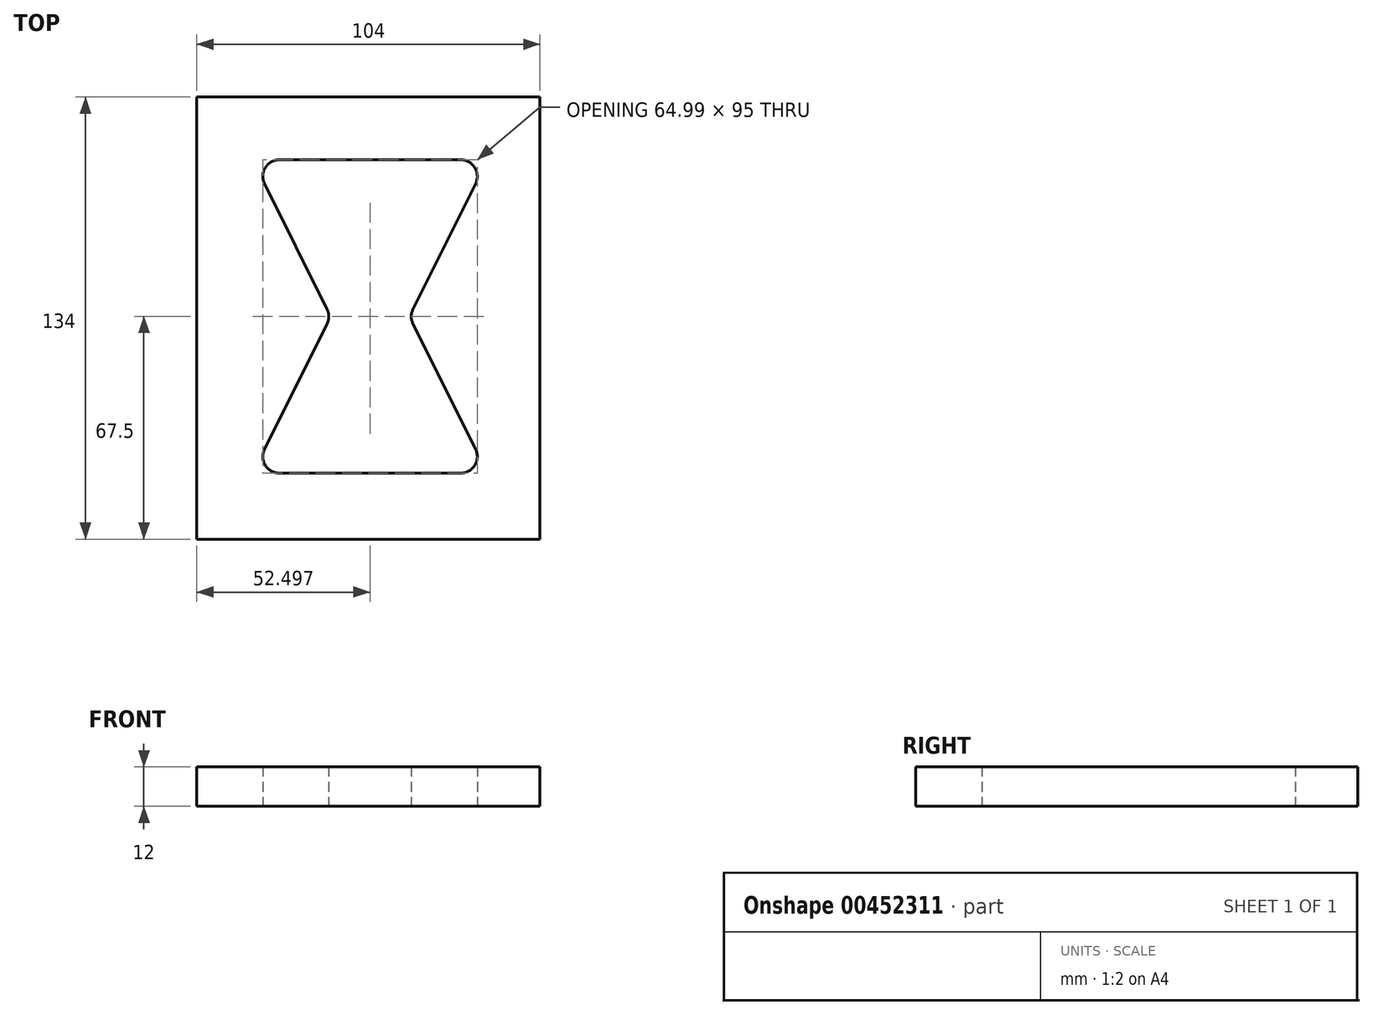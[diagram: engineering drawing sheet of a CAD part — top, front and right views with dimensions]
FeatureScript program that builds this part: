
annotation { "Feature Type Name" : "Feature", "Feature Type Description" : "" }
export const myFeature = defineFeature(function(context is Context, id is Id, definition is map)
    precondition{}
    {
        {
            var Q0;
            Q0=qCreatedBy(makeId("Top.planeOp"),FACE);
            var sketch = newSketch(context, id + "F0", { "sketchPlane" : qUnion([Q0])});
            skLineSegment(sketch, "E0", {"start": v(-3.13, 0) * mm, "end": v(-58.13, 0) * mm});
            skLineSegment(sketch, "E1", {"start": v(-58.13, 95) * mm, "end": v(-3.13, 95) * mm});
            skLineSegment(sketch, "E2", {"start": v(-18.72, 47.5) * mm, "end": v(-42.55, 47.5) * mm});
            skLineSegment(sketch, "E3", {"start": v(1.34, 87.77) * mm, "end": v(-17.6, 49.73) * mm});
            skLineSegment(sketch, "E4", {"start": v(-62.6, 87.77) * mm, "end": v(-43.66, 49.73) * mm});
            skLineSegment(sketch, "E5", {"start": v(-43.66, 45.27) * mm, "end": v(-62.6, 7.23) * mm});
            skLineSegment(sketch, "E6", {"start": v(-17.6, 45.27) * mm, "end": v(1.34, 7.23) * mm});
            skArc(sketch, "E7.filletArc", {"start": v(-62.6, 7.23) * mm, "mid": v(-62.38, 2.37) * mm, "end": v(-58.13, 0) * mm});
            skPoint(sketch, "E8.newPointA", {"position": v(1.87, 0) * mm});
            skArc(sketch, "E8.filletArc", {"start": v(-3.13, 0) * mm, "mid": v(1.12, 2.37) * mm, "end": v(1.34, 7.23) * mm});
            skArc(sketch, "E9.filletArc", {"start": v(1.34, 87.77) * mm, "mid": v(1.12, 92.63) * mm, "end": v(-3.13, 95) * mm});
            skArc(sketch, "E10.filletArc", {"start": v(-58.13, 95) * mm, "mid": v(-62.38, 92.63) * mm, "end": v(-62.6, 87.77) * mm});
            skPoint(sketch, "E11.visualSharp", {"position": v(-42.55, 47.5) * mm});
            skArc(sketch, "E11.filletArc", {"start": v(-43.66, 45.27) * mm, "mid": v(-43.13, 47.5) * mm, "end": v(-43.66, 49.73) * mm});
            skPoint(sketch, "E12.visualSharp", {"position": v(-18.72, 47.5) * mm});
            skArc(sketch, "E12.filletArc", {"start": v(-17.6, 49.73) * mm, "mid": v(-18.13, 47.5) * mm, "end": v(-17.6, 45.27) * mm});
            skLineSegment(sketch, "E13", {"start": v(1.87, 5) * mm, "end": v(1.87, 90) * mm});
            skLineSegment(sketch, "E14", {"start": v(-63.13, 5) * mm, "end": v(-63.13, 90) * mm});
            skLineSegment(sketch, "E15.bottom", {"start": v(-83.13, -20) * mm, "end": v(20.87, -20) * mm});
            skLineSegment(sketch, "E15.top", {"start": v(-83.13, 114) * mm, "end": v(20.87, 114) * mm});
            skLineSegment(sketch, "E15.left", {"start": v(-83.13, -20) * mm, "end": v(-83.13, 114) * mm});
            skLineSegment(sketch, "E15.right", {"start": v(20.87, -20) * mm, "end": v(20.87, 114) * mm});
            skSolve(sketch);
        }
        {
            var Q0;
            Q0=makeQuery(id+"F0.imprint","IMPRINT",FACE,{"disambiguationData":[TD([[makeQuery(id+"F0.imprint","IMPRINT",EDGE,{"derivedFrom":sQuery(id+"F0.wireOp",EDGE,"E1")}),-1.0]])]});
            var Q1;
            {var subQ0=sQuery(id+"F0.wireOp",EDGE,"E0");Q1=makeQuery(id+"F0.imprint","IMPRINT",FACE,{"disambiguationData":[TD([[makeQuery(id+"F0.imprint","IMPRINT",EDGE,{"derivedFrom":subQ0}),-1.0]])]});}
            extrude(context, id + "F1", {"entities" : qUnion([Q0, Q1]), "depth" : 12 * mm, "offsetDistance" : 25 * mm});
        }
        {
            var Q0;
            {var subQ4=sQuery(id+"F0.wireOp",EDGE,"E0");Q0=makeQuery(id+"F0.imprint","IMPRINT",FACE,{"disambiguationData":[TD([[makeQuery(id+"F0.imprint","IMPRINT",EDGE,{"derivedFrom":subQ4}),1.0]])]});}
            var Q1;
            {var subQ4=sQuery(id+"F0.wireOp",EDGE,"E4");Q1=makeQuery(id+"F0.imprint","IMPRINT",FACE,{"disambiguationData":[TD([[makeQuery(id+"F0.imprint","IMPRINT",EDGE,{"derivedFrom":subQ4}),-1.0]])]});}
            var Q2;
            {var subQ4=sQuery(id+"F0.wireOp",EDGE,"E3");Q2=makeQuery(id+"F0.imprint","IMPRINT",FACE,{"disambiguationData":[TD([[makeQuery(id+"F0.imprint","IMPRINT",EDGE,{"derivedFrom":subQ4}),1.0]])]});}
            extrude(context, id + "F2", {"entities" : qUnion([Q0, Q1, Q2]), "depth" : 12 * mm, "offsetDistance" : 25 * mm});
        }
    });
